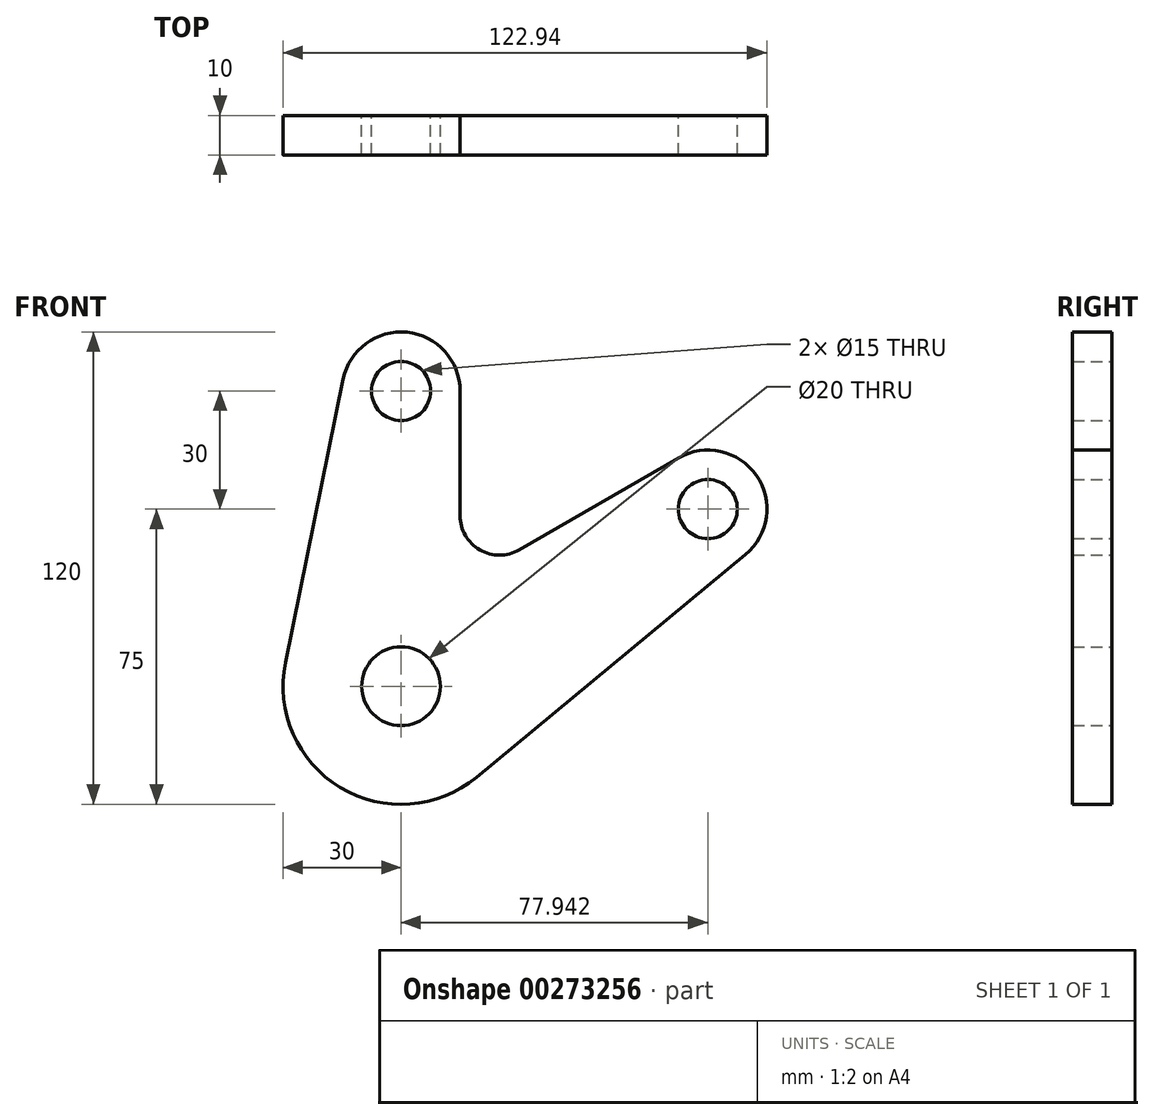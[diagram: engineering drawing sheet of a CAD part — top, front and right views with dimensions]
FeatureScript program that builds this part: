
annotation { "Feature Type Name" : "Feature", "Feature Type Description" : "" }
export const myFeature = defineFeature(function(context is Context, id is Id, definition is map)
    precondition{}
    {
        {
            var Q0;
            Q0=qCreatedBy(makeId("Front.planeOp"),FACE);
            var sketch = newSketch(context, id + "F0", { "sketchPlane" : qUnion([Q0])});
            skCircle(sketch, "E0", {"center": v(0, 0) * mm, "radius": 10 * mm});
            skLineSegment(sketch, "E1", {"start": v(0, 0) * mm, "end": v(77.94, 45) * mm, "construction": true});
            skLineSegment(sketch, "E2", {"start": v(0, 0) * mm, "end": v(0, 75) * mm, "construction": true});
            skCircle(sketch, "E3", {"center": v(77.94, 45) * mm, "radius": 7.5 * mm});
            skCircle(sketch, "E4", {"center": v(0, 75) * mm, "radius": 7.5 * mm});
            skLineSegment(sketch, "E5", {"start": v(-14.7, 78) * mm, "end": v(-29.4, 6) * mm});
            skLineSegment(sketch, "E6", {"start": v(87.5, 33.44) * mm, "end": v(19.12, -23.12) * mm});
            skLineSegment(sketch, "E7", {"start": v(70.44, 58) * mm, "end": v(30, 34.64) * mm});
            skLineSegment(sketch, "E8", {"start": v(15, 75) * mm, "end": v(15, 43.3) * mm});
            skArc(sketch, "E9", {"start": v(-29.4, 6) * mm, "mid": v(-15.44, -25.72) * mm, "end": v(19.12, -23.12) * mm});
            skArc(sketch, "E10", {"start": v(-14.7, 78) * mm, "mid": v(1.5, 89.92) * mm, "end": v(15, 75) * mm});
            skArc(sketch, "E11", {"start": v(70.44, 58) * mm, "mid": v(90.26, 53.56) * mm, "end": v(87.5, 33.44) * mm});
            skPoint(sketch, "E12.visualSharp", {"position": v(15, 25.98) * mm});
            skArc(sketch, "E12.filletArc", {"start": v(15, 43.3) * mm, "mid": v(20, 34.64) * mm, "end": v(30, 34.64) * mm});
            skSolve(sketch);
        }
        {
            var Q0;
            Q0 = qSketchRegion(id + "F0", true);
            extrude(context, id + "F1", {"entities" : qUnion([Q0]), "depth" : 10 * mm});
        }
    });
